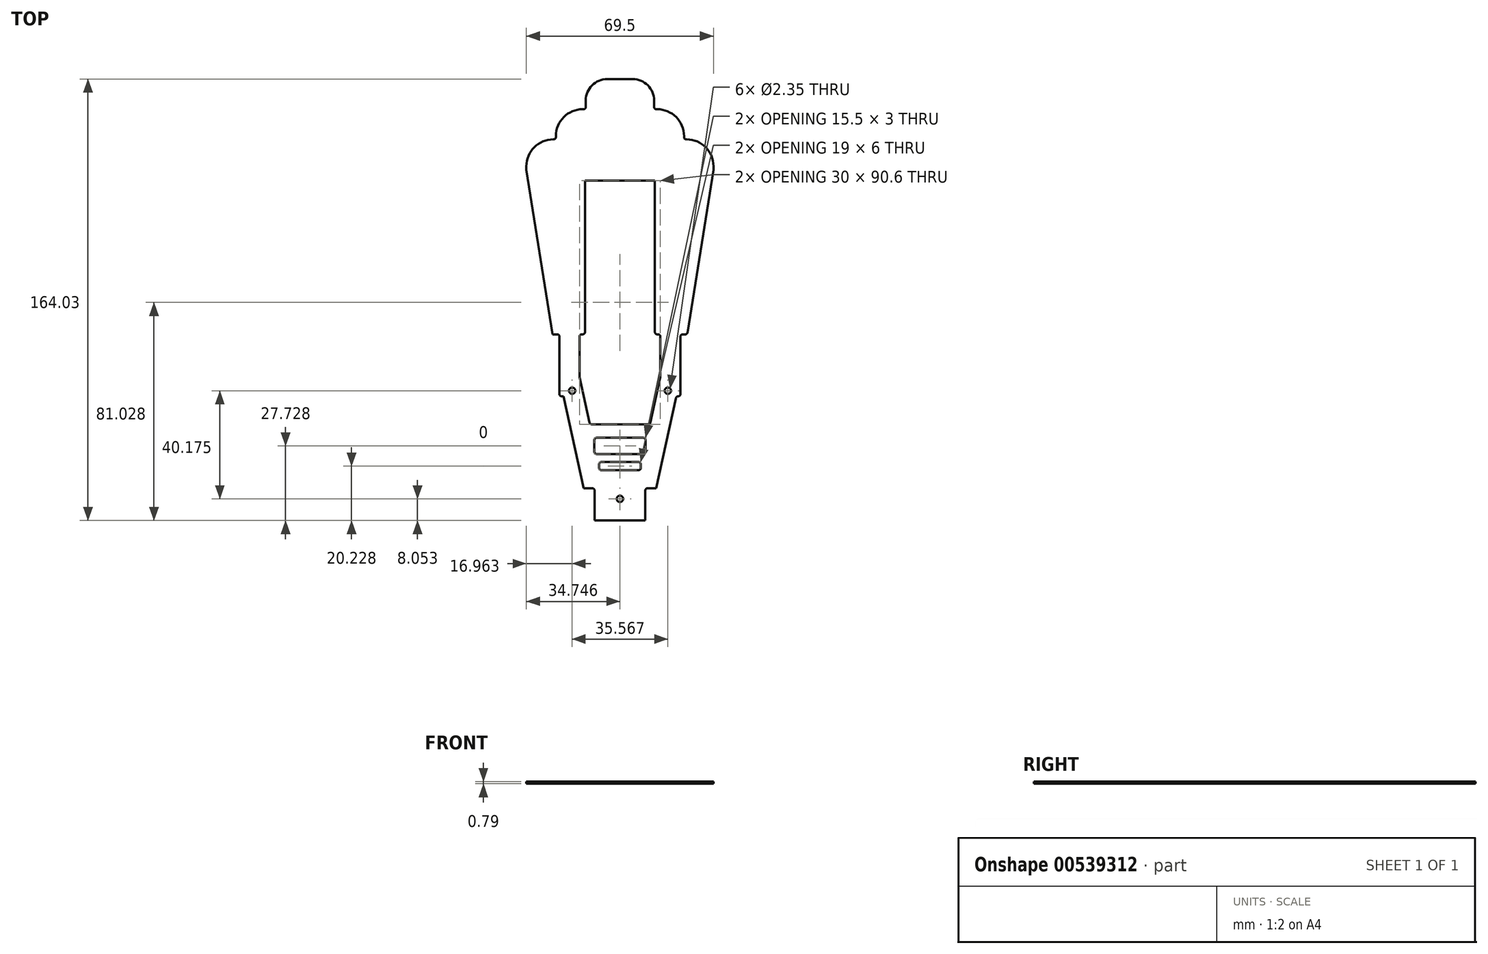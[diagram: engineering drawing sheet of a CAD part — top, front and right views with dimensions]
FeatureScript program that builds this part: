
annotation { "Feature Type Name" : "Feature", "Feature Type Description" : "" }
export const myFeature = defineFeature(function(context is Context, id is Id, definition is map)
    precondition{}
    {
        {
            var Q0;
            Q0=qCreatedBy(makeId("Top.planeOp"),FACE);
            var sketch = newSketch(context, id + "F0", { "sketchPlane" : qUnion([Q0])});
            skLineSegment(sketch, "E0", {"start": v(-95.62, 124.25) * mm, "end": v(-95.62, -39.78) * mm, "construction": true});
            skLineSegment(sketch, "E1", {"start": v(-26.12, 124.25) * mm, "end": v(-26.12, -39.78) * mm, "construction": true});
            skLineSegment(sketch, "E2", {"start": v(-95.62, 124.25) * mm, "end": v(-26.12, 124.25) * mm, "construction": true});
            skLineSegment(sketch, "E3", {"start": v(-95.62, -39.78) * mm, "end": v(-26.12, -39.78) * mm, "construction": true});
            skLineSegment(sketch, "E4", {"start": v(-73.87, 86.55) * mm, "end": v(-47.87, 86.55) * mm});
            skLineSegment(sketch, "E5", {"start": v(-60.87, 124.25) * mm, "end": v(-60.87, -39.78) * mm, "construction": true});
            skLineSegment(sketch, "E6", {"start": v(-73.87, 86.55) * mm, "end": v(-73.87, 30.2) * mm});
            skLineSegment(sketch, "E7", {"start": v(-74.67, 29.4) * mm, "end": v(-75.08, 29.4) * mm});
            skLineSegment(sketch, "E8", {"start": v(-75.87, 28.6) * mm, "end": v(-75.87, 13.52) * mm});
            skLineSegment(sketch, "E9", {"start": v(-75.87, 13.52) * mm, "end": v(-72.12, -3.43) * mm});
            skLineSegment(sketch, "E10", {"start": v(-71.35, -4.05) * mm, "end": v(-50.4, -4.05) * mm});
            skLineSegment(sketch, "E11", {"start": v(-49.62, -3.43) * mm, "end": v(-45.87, 13.52) * mm});
            skLineSegment(sketch, "E12", {"start": v(-45.87, 13.52) * mm, "end": v(-45.87, 28.6) * mm});
            skLineSegment(sketch, "E13", {"start": v(-46.67, 29.4) * mm, "end": v(-47.08, 29.4) * mm});
            skLineSegment(sketch, "E14", {"start": v(-47.87, 30.2) * mm, "end": v(-47.87, 86.55) * mm});
            skLineSegment(sketch, "E15", {"start": v(-95.62, 90.63) * mm, "end": v(-85.87, 29.4) * mm});
            skLineSegment(sketch, "E16", {"start": v(-85.87, 29.4) * mm, "end": v(-84.17, 29.4) * mm});
            skLineSegment(sketch, "E17", {"start": v(-83.37, 28.6) * mm, "end": v(-83.37, 7.2) * mm});
            skLineSegment(sketch, "E18", {"start": v(-82.58, 6.4) * mm, "end": v(-81.87, 6.4) * mm});
            skLineSegment(sketch, "E19", {"start": v(-81.87, 6.4) * mm, "end": v(-74.31, -27.78) * mm});
            skLineSegment(sketch, "E20", {"start": v(-74.31, -27.78) * mm, "end": v(-71.1, -27.78) * mm});
            skLineSegment(sketch, "E21", {"start": v(-70.31, -28.57) * mm, "end": v(-70.31, -39.78) * mm});
            skLineSegment(sketch, "E22", {"start": v(-70.31, -39.78) * mm, "end": v(-51.43, -39.78) * mm});
            skLineSegment(sketch, "E23", {"start": v(-51.43, -39.78) * mm, "end": v(-51.43, -28.57) * mm});
            skLineSegment(sketch, "E24", {"start": v(-50.64, -27.78) * mm, "end": v(-47.43, -27.78) * mm});
            skLineSegment(sketch, "E25", {"start": v(-47.43, -27.78) * mm, "end": v(-40.01, 5.78) * mm});
            skLineSegment(sketch, "E26", {"start": v(-39.24, 6.4) * mm, "end": v(-39.17, 6.4) * mm});
            skLineSegment(sketch, "E27", {"start": v(-38.37, 7.2) * mm, "end": v(-38.37, 28.6) * mm});
            skLineSegment(sketch, "E28", {"start": v(-37.58, 29.4) * mm, "end": v(-36.55, 29.4) * mm});
            skLineSegment(sketch, "E29", {"start": v(-35.77, 30.07) * mm, "end": v(-26.12, 90.63) * mm});
            skLineSegment(sketch, "E30", {"start": v(-73.57, 116.25) * mm, "end": v(-73.57, 113.84) * mm});
            skLineSegment(sketch, "E31", {"start": v(-74.37, 113.04) * mm, "end": v(-74.69, 113.04) * mm});
            skLineSegment(sketch, "E32", {"start": v(-84.69, 103.04) * mm, "end": v(-84.69, 102.63) * mm});
            skLineSegment(sketch, "E33", {"start": v(-85.48, 101.83) * mm, "end": v(-85.62, 101.83) * mm});
            skLineSegment(sketch, "E34", {"start": v(-95.62, 91.83) * mm, "end": v(-95.62, 90.63) * mm});
            skLineSegment(sketch, "E35", {"start": v(-65.57, 124.25) * mm, "end": v(-56.17, 124.25) * mm});
            skLineSegment(sketch, "E36", {"start": v(-48.17, 116.25) * mm, "end": v(-48.17, 113.84) * mm});
            skLineSegment(sketch, "E37", {"start": v(-47.38, 113.04) * mm, "end": v(-47.06, 113.04) * mm});
            skLineSegment(sketch, "E38", {"start": v(-37.06, 103.04) * mm, "end": v(-37.06, 102.63) * mm});
            skLineSegment(sketch, "E39", {"start": v(-36.27, 101.83) * mm, "end": v(-36.12, 101.83) * mm});
            skLineSegment(sketch, "E40", {"start": v(-26.12, 91.83) * mm, "end": v(-26.12, 90.63) * mm});
            skLineSegment(sketch, "E41.bottom", {"start": v(-52.17, -9.05) * mm, "end": v(-69.58, -9.05) * mm});
            skLineSegment(sketch, "E41.top", {"start": v(-52.17, -15.05) * mm, "end": v(-69.58, -15.05) * mm});
            skLineSegment(sketch, "E41.left", {"start": v(-51.37, -9.85) * mm, "end": v(-51.37, -14.26) * mm});
            skLineSegment(sketch, "E41.right", {"start": v(-70.37, -9.85) * mm, "end": v(-70.37, -14.26) * mm});
            skPoint(sketch, "E41.middle", {"position": v(-60.87, -12.05) * mm});
            skLineSegment(sketch, "E42.bottom", {"start": v(-53.92, -18.05) * mm, "end": v(-67.83, -18.05) * mm});
            skLineSegment(sketch, "E42.top", {"start": v(-53.92, -21.05) * mm, "end": v(-67.83, -21.05) * mm});
            skLineSegment(sketch, "E42.left", {"start": v(-53.12, -18.85) * mm, "end": v(-53.12, -20.26) * mm});
            skLineSegment(sketch, "E42.right", {"start": v(-68.62, -18.85) * mm, "end": v(-68.62, -20.26) * mm});
            skPoint(sketch, "E42.middle", {"position": v(-60.87, -19.55) * mm});
            skCircle(sketch, "E43", {"center": v(-60.87, -31.73) * mm, "radius": 1.18 * mm});
            skCircle(sketch, "E44", {"center": v(-78.66, 8.45) * mm, "radius": 1.18 * mm});
            skCircle(sketch, "E45", {"center": v(-43.09, 8.45) * mm, "radius": 1.18 * mm});
            skCircle(sketch, "E46", {"center": v(-78.66, 8.45) * mm, "radius": 3.81 * mm, "construction": true});
            skPoint(sketch, "E47.visualSharp", {"position": v(-48.17, 124.25) * mm});
            skArc(sketch, "E47.filletArc", {"start": v(-48.17, 116.25) * mm, "mid": v(-50.52, 121.9) * mm, "end": v(-56.17, 124.25) * mm});
            skPoint(sketch, "E48.visualSharp", {"position": v(-73.57, 124.25) * mm});
            skArc(sketch, "E48.filletArc", {"start": v(-65.57, 124.25) * mm, "mid": v(-71.23, 121.9) * mm, "end": v(-73.57, 116.25) * mm});
            skPoint(sketch, "E49.visualSharp", {"position": v(-73.57, 113.04) * mm});
            skArc(sketch, "E49.filletArc", {"start": v(-74.37, 113.04) * mm, "mid": v(-73.8, 113.27) * mm, "end": v(-73.57, 113.84) * mm});
            skPoint(sketch, "E50.visualSharp", {"position": v(-48.17, 113.04) * mm});
            skArc(sketch, "E50.filletArc", {"start": v(-48.17, 113.84) * mm, "mid": v(-47.94, 113.27) * mm, "end": v(-47.38, 113.04) * mm});
            skPoint(sketch, "E51.visualSharp", {"position": v(-37.06, 101.83) * mm});
            skArc(sketch, "E51.filletArc", {"start": v(-37.06, 102.63) * mm, "mid": v(-36.83, 102.07) * mm, "end": v(-36.27, 101.83) * mm});
            skPoint(sketch, "E52.visualSharp", {"position": v(-84.69, 101.83) * mm});
            skArc(sketch, "E52.filletArc", {"start": v(-85.48, 101.83) * mm, "mid": v(-84.92, 102.07) * mm, "end": v(-84.69, 102.63) * mm});
            skPoint(sketch, "E53.visualSharp", {"position": v(-83.37, 29.4) * mm});
            skArc(sketch, "E53.filletArc", {"start": v(-83.37, 28.6) * mm, "mid": v(-83.6, 29.17) * mm, "end": v(-84.17, 29.4) * mm});
            skPoint(sketch, "E54.visualSharp", {"position": v(-75.87, 29.4) * mm});
            skArc(sketch, "E54.filletArc", {"start": v(-75.08, 29.4) * mm, "mid": v(-75.64, 29.17) * mm, "end": v(-75.87, 28.6) * mm});
            skPoint(sketch, "E55.visualSharp", {"position": v(-45.87, 29.4) * mm});
            skArc(sketch, "E55.filletArc", {"start": v(-45.87, 28.6) * mm, "mid": v(-46.1, 29.17) * mm, "end": v(-46.67, 29.4) * mm});
            skPoint(sketch, "E56.visualSharp", {"position": v(-38.37, 29.4) * mm});
            skArc(sketch, "E56.filletArc", {"start": v(-37.58, 29.4) * mm, "mid": v(-38.14, 29.17) * mm, "end": v(-38.37, 28.6) * mm});
            skPoint(sketch, "E57.visualSharp", {"position": v(-39.87, 6.4) * mm});
            skArc(sketch, "E57.filletArc", {"start": v(-39.24, 6.4) * mm, "mid": v(-39.73, 6.22) * mm, "end": v(-40.01, 5.78) * mm});
            skPoint(sketch, "E58.visualSharp", {"position": v(-51.43, -27.78) * mm});
            skArc(sketch, "E58.filletArc", {"start": v(-50.64, -27.78) * mm, "mid": v(-51.2, -28) * mm, "end": v(-51.43, -28.57) * mm});
            skPoint(sketch, "E59.visualSharp", {"position": v(-70.31, -27.78) * mm});
            skArc(sketch, "E59.filletArc", {"start": v(-70.31, -28.57) * mm, "mid": v(-70.55, -28) * mm, "end": v(-71.1, -27.78) * mm});
            skPoint(sketch, "E60.visualSharp", {"position": v(-68.62, -21.05) * mm});
            skArc(sketch, "E60.filletArc", {"start": v(-68.62, -20.26) * mm, "mid": v(-68.4, -20.82) * mm, "end": v(-67.83, -21.05) * mm});
            skPoint(sketch, "E61.visualSharp", {"position": v(-53.12, -21.05) * mm});
            skArc(sketch, "E61.filletArc", {"start": v(-53.92, -21.05) * mm, "mid": v(-53.36, -20.82) * mm, "end": v(-53.12, -20.26) * mm});
            skPoint(sketch, "E62.visualSharp", {"position": v(-53.12, -18.05) * mm});
            skArc(sketch, "E62.filletArc", {"start": v(-53.12, -18.85) * mm, "mid": v(-53.36, -18.28) * mm, "end": v(-53.92, -18.05) * mm});
            skPoint(sketch, "E63.visualSharp", {"position": v(-68.62, -18.05) * mm});
            skArc(sketch, "E63.filletArc", {"start": v(-67.83, -18.05) * mm, "mid": v(-68.4, -18.28) * mm, "end": v(-68.62, -18.85) * mm});
            skPoint(sketch, "E64.visualSharp", {"position": v(-70.37, -15.05) * mm});
            skArc(sketch, "E64.filletArc", {"start": v(-70.37, -14.26) * mm, "mid": v(-70.14, -14.82) * mm, "end": v(-69.58, -15.05) * mm});
            skPoint(sketch, "E65.visualSharp", {"position": v(-70.37, -9.05) * mm});
            skArc(sketch, "E65.filletArc", {"start": v(-69.58, -9.05) * mm, "mid": v(-70.14, -9.28) * mm, "end": v(-70.37, -9.85) * mm});
            skPoint(sketch, "E66.visualSharp", {"position": v(-51.37, -9.05) * mm});
            skArc(sketch, "E66.filletArc", {"start": v(-51.37, -9.85) * mm, "mid": v(-51.6, -9.28) * mm, "end": v(-52.17, -9.05) * mm});
            skPoint(sketch, "E67.visualSharp", {"position": v(-51.37, -15.05) * mm});
            skArc(sketch, "E67.filletArc", {"start": v(-52.17, -15.05) * mm, "mid": v(-51.6, -14.82) * mm, "end": v(-51.37, -14.26) * mm});
            skPoint(sketch, "E68.visualSharp", {"position": v(-71.99, -4.05) * mm});
            skArc(sketch, "E68.filletArc", {"start": v(-72.12, -3.43) * mm, "mid": v(-71.85, -3.88) * mm, "end": v(-71.35, -4.05) * mm});
            skPoint(sketch, "E69.visualSharp", {"position": v(-49.76, -4.05) * mm});
            skArc(sketch, "E69.filletArc", {"start": v(-50.4, -4.05) * mm, "mid": v(-49.9, -3.88) * mm, "end": v(-49.62, -3.43) * mm});
            skPoint(sketch, "E70.visualSharp", {"position": v(-73.87, 29.4) * mm});
            skArc(sketch, "E70.filletArc", {"start": v(-74.67, 29.4) * mm, "mid": v(-74.1, 29.63) * mm, "end": v(-73.87, 30.2) * mm});
            skPoint(sketch, "E71.visualSharp", {"position": v(-47.87, 29.4) * mm});
            skArc(sketch, "E71.filletArc", {"start": v(-47.87, 30.2) * mm, "mid": v(-47.64, 29.63) * mm, "end": v(-47.08, 29.4) * mm});
            skPoint(sketch, "E72.visualSharp", {"position": v(-38.37, 6.4) * mm});
            skArc(sketch, "E72.filletArc", {"start": v(-39.17, 6.4) * mm, "mid": v(-38.6, 6.63) * mm, "end": v(-38.37, 7.2) * mm});
            skPoint(sketch, "E73.visualSharp", {"position": v(-83.37, 6.4) * mm});
            skArc(sketch, "E73.filletArc", {"start": v(-83.37, 7.2) * mm, "mid": v(-83.14, 6.63) * mm, "end": v(-82.58, 6.4) * mm});
            skPoint(sketch, "E74.visualSharp", {"position": v(-35.87, 29.4) * mm});
            skArc(sketch, "E74.filletArc", {"start": v(-36.55, 29.4) * mm, "mid": v(-36.04, 29.59) * mm, "end": v(-35.77, 30.07) * mm});
            skPoint(sketch, "E75.visualSharp", {"position": v(-37.06, 113.04) * mm});
            skArc(sketch, "E75.filletArc", {"start": v(-37.06, 103.04) * mm, "mid": v(-39.99, 110.11) * mm, "end": v(-47.06, 113.04) * mm});
            skPoint(sketch, "E76.visualSharp", {"position": v(-84.69, 113.04) * mm});
            skArc(sketch, "E76.filletArc", {"start": v(-74.69, 113.04) * mm, "mid": v(-81.76, 110.11) * mm, "end": v(-84.69, 103.04) * mm});
            skPoint(sketch, "E77.visualSharp", {"position": v(-26.12, 101.83) * mm});
            skArc(sketch, "E77.filletArc", {"start": v(-26.12, 91.83) * mm, "mid": v(-29.05, 98.9) * mm, "end": v(-36.12, 101.83) * mm});
            skPoint(sketch, "E78.visualSharp", {"position": v(-95.62, 101.83) * mm});
            skArc(sketch, "E78.filletArc", {"start": v(-85.62, 101.83) * mm, "mid": v(-92.7, 98.9) * mm, "end": v(-95.62, 91.83) * mm});
            skLineSegment(sketch, "E79.bottom", {"start": v(-16.42, 156.54) * mm, "end": v(-105.32, 156.54) * mm, "construction": true});
            skLineSegment(sketch, "E79.top", {"start": v(-16.42, -72.06) * mm, "end": v(-105.32, -72.06) * mm, "construction": true});
            skLineSegment(sketch, "E79.left", {"start": v(-16.42, 156.54) * mm, "end": v(-16.42, -72.06) * mm, "construction": true});
            skLineSegment(sketch, "E79.right", {"start": v(-105.32, 156.54) * mm, "end": v(-105.32, -72.06) * mm, "construction": true});
            skPoint(sketch, "E79.middle", {"position": v(-60.87, 42.24) * mm});
            skSolve(sketch);
        }
        {
            var Q0;
            Q0 = qSketchRegion(id + "F0", true);
            extrude(context, id + "F1", {"entities" : qUnion([Q0]), "depth" : 0.8 * mm, "offsetDistance" : 25.4 * mm});
        }
    });
